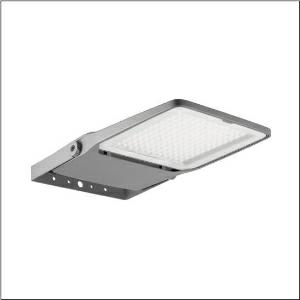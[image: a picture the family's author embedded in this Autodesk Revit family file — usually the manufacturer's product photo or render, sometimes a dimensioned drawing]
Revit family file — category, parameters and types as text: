
# Revit family: floodlight_fl_20_midi___pl52_5xa7682e1d2ac_40bd
name_source: partatom
category: Lighting Fixtures
units: mm (PartAtom-declared; Revit-internal decimal feet)

## family parameters
Cut with Voids When Loaded = No
Host = Face
Light Source = No
Part Type = Normal
Room Calculation Point = No
Round Connector Dimension = Use Diameter
Shared = No

## types (1)
- --- (1 x LED 3000K / CRI = 80 (unbekannt), 21030 lm, 3000K)
    Apparent Load = 208 VA
    CIE Flux Codes = 27 59 98 100 100
    Color Rendering = 80
    Color Temperature = 3000K
    Default Elevation = 1800 mm
    Description = Floodlight FL 20 midi, floodlight, primary light control with lens, of plastic, primary optical cover: protective disc, of toughened safety glass, transparent, light distribution: PL52, light emission: direct distribution, primary light characteristic: asymmetric, installation type: surface-mounted, LED High Power LED, rated luminous flux: 21.030 lm, light colour: 830, colour temperature: 3000K, control gear: ECG Plus, control: flexible luminous flux parameterisation, time-dependent luminous flux control, digital communication interface, power reduction, overheat protection, electronic power reduction, with terminal, 5-pole, max. 2.5mm², mains connection: 220..240V, AC, 50/60Hz, rated input power: 208W, LED unit, of diecast aluminium, powder-coated, Siteco® metallic grey (DB 702S), length: 731 mm, width: 450 mm, height: 76mm, housing frame, of diecast aluminium, powder-coated, Siteco® metallic grey (DB 702S), wall fastening, of steel, powder-coated, Siteco® metallic grey (DB 702S), DALIprotection rating (complete): IP66, insulation class (complete): insulation class II (safety insulation), certification: CE, ENEC, VDE, protection symbol: D, permissible ambient temperature for indoor applications: -40..+40°C, permissible ambient temperature for outdoor applications: -40..+50°C, standard: DIN EN 12944, packaging unit: 1 piece

Light Distribution: PL52
    Height = 76 mm
    Lamp = 1 x LED 3000K / CRI >= 80 (unbekannt)
    Lamp Light Flux = 21030 lm
    Lamp count = 1
    Length = 731 mm
    Luminous efficacy = 101 lm/W
    Manufacturer = Siteco
    ModVariant = No
    Model = 5XA7682E1D2AC
    Number of Poles = 1
    OnlyDefault = Yes
    Power Factor = 1
    Product Name = Floodlight FL 20 midi | PL52
    Product group = floodlight | pylon top
    ProductGroupID = 6101
    Protection Class = Protection class II
    Protection Degree = IP 66
    RLX_Detail_Level = 1
    RlxData = <blob elided: 92309 chars, md5=49644f5c>
    Socket = socket
    Standby Power = 0 W
    System Light Flux = 21030 lm
    System Power = 208 W
    Type Comments = factory setting: luminous flux: 100 % | dim-lin: 254 | 484 mA
    Type Image = l_1005944.jpg
    URL = http://relux.com
    VarID = @adj_143043
    Voltage = 0 V
    Weight = 0.00 kg
    Width = 450 mm

## geometry (parser evidence)
native form markers: Blend x4, Sweep x14
no freeform markers — native parametric forms only
